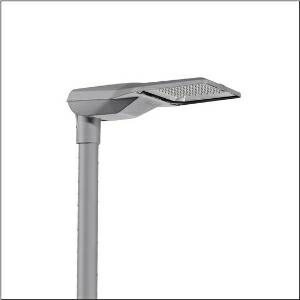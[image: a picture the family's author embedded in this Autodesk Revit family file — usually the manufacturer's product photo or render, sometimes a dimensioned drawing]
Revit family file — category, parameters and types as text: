
# Revit family: streetlight_sl_21_iq_midi___p0_8ab_5xe3r31d08mb_e13a
name_source: partatom
category: Lighting Fixtures
units: mm (PartAtom-declared; Revit-internal decimal feet)

## family parameters
Cut with Voids When Loaded = No
Host = Face
Light Source = No
Part Type = Normal
Room Calculation Point = No
Round Connector Dimension = Use Diameter
Shared = No

## types (1)
- --- (1 x LED, 16930 lm, 146.7 W, 3000K)
    Apparent Load = 147 VA
    CIE Flux Codes = 36 71 98 100 100
    Color Rendering = 70
    Color Temperature = 3000K
    Default Elevation = 1800 mm
    Description = Streetlight SL 21 iQ midi, mast luminaire, primary light control with lens, of PMMA, primary optical cover: cover, of toughened safety glass, transparent, light distribution: P0.8aB, light emission: direct distribution, primary light characteristic: asymmetric, installation type: post-top, side-entry, LED, High Power LED, rated luminous flux: 16.930lm, luminous efficacy: 115lm/W, light colour: 730, colour temperature: 3000K, control gear: iQ-Comfort, control: pre-setting: linear dimming characteristic, Auto-Match, Temp-Guard, Lumen-Switch, Night-Set, Smart-Wire, Light-Fading, Desk-Remote (wireless, voltage-free reading and setting of iQ features in the workshop via application-optimized NFC function/RFID function), optimised constant luminous flux control (CLO 2.0), mains connection: 230..240V, AC, 50/60Hz, start of lifetime: 147W, end of service life: 161W, reduction: 62W, luminaire housing, of diecast aluminium, powder-coated, Siteco® metallic grey (DB 702S), corrosivity category C5 mid according to DIN EN ISO 12944, please order mast flange separately, inclination adjustable: 0°, 5°, 10°, 15°, sealing non-destructively replaceable, multi-level sealing system, length: 644mm, width: 335mm, height: 110mm, mast flange for spigot size: 42mm (side-entry): 5XC10008XM4, 60/48mm (side-entry/post-top): 5XC10108XM2, 76/60mm (side-entry/post-top): 5XC10108XM1, mounting height: 4..8m, protection rating (complete): IP66, insulation class (complete): insulation class II (safety insulation), certification: CE, ENEC, ENEC+, VDE, impact resistance: IK10, permissible operating ambient temperature for outdoor applications: -40..+50°C, standard-compliant lighting for roads and squares, packaging unit: 1 piece

Light Distribution: P0.8aB
    Height = 111 mm
    Lamp = 1 x LED
    Lamp Light Flux = 16930 lm
    Lamp Power = 146.7 W
    Lamp count = 1
    Length = 644 mm
    Luminous efficacy = 115 lm/W
    Manufacturer = Siteco
    ModVariant = No
    Model = 5XE3R31D08MB
    Number of Poles = 1
    OnlyDefault = Yes
    Power Factor = 1
    Product Name = Streetlight SL 21 iQ midi | P0.8aB
    Product group = mast luminaire | pylon top
    ProductGroupID = 6100
    Protection Class = Protection class II
    Protection Degree = IP 66
    RLX_Detail_Level = 1
    RLX_Emergency_Light_Flux = 0 lm
    RLX_Emergency_Type = 0
    RLX_Emergency_Type_DB = No
    RlxData = <blob elided: 90597 chars, md5=b6ff4034>
    Socket = socket
    Standby Power = 0 W
    System Light Flux = 16931 lm
    System Power = 147 W
    Type Comments = factory setting: luminous flux: 100 % | dim-lin: 254 | 753 mA
    Type Image = l_1004298.jpg
    URL = http://relux.com
    VarID = @adj_095931
    Voltage = 0 V
    Weight = 0.00 kg
    Width = 336 mm

## geometry (parser evidence)
native form markers: Blend x4, Sweep x12
no freeform markers — native parametric forms only
